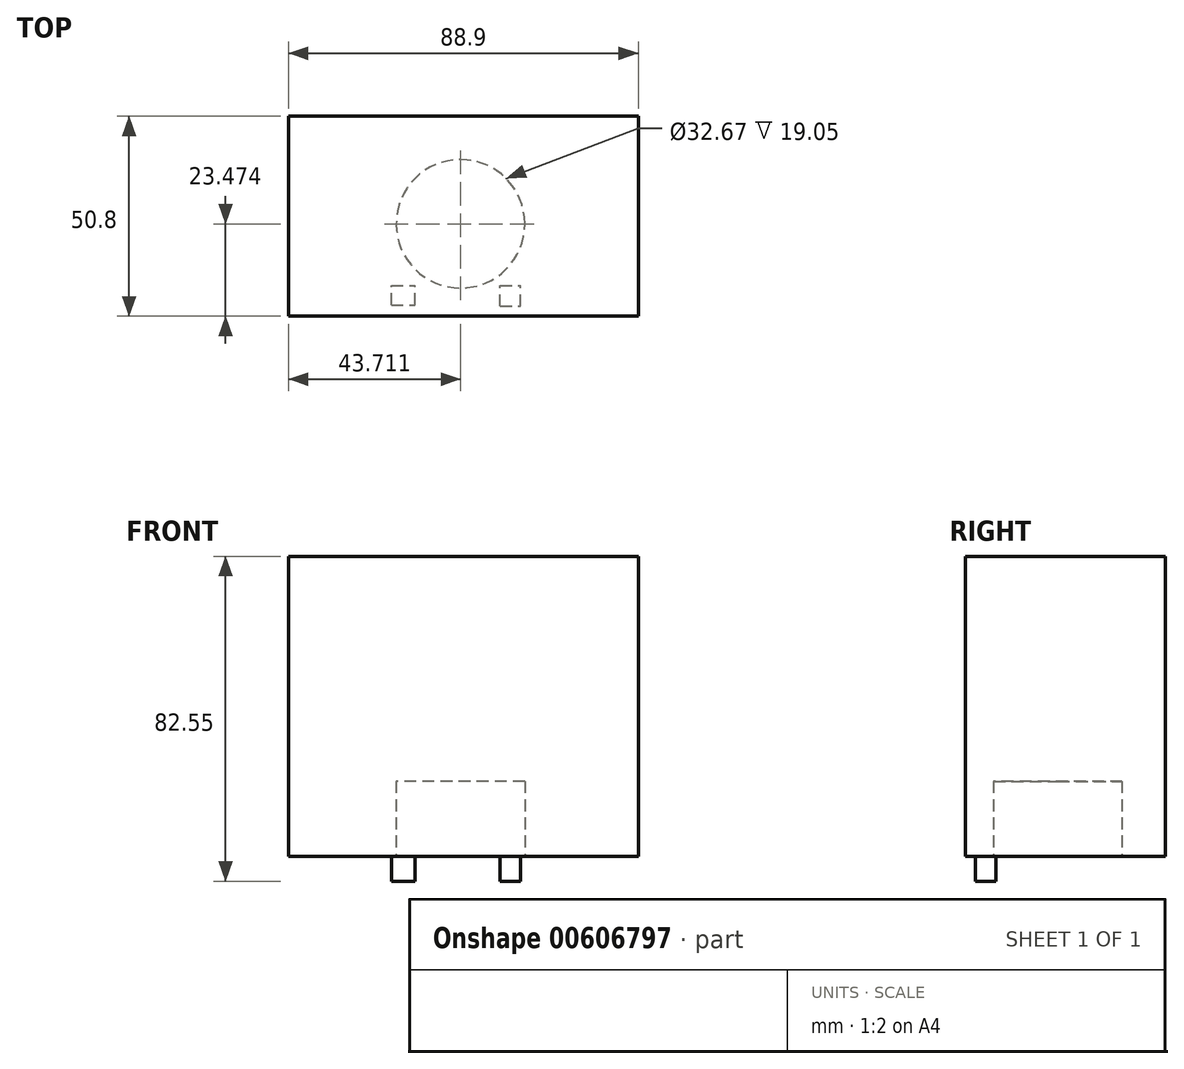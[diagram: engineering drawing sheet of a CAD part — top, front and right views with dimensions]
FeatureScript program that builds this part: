
annotation { "Feature Type Name" : "Feature", "Feature Type Description" : "" }
export const myFeature = defineFeature(function(context is Context, id is Id, definition is map)
    precondition{}
    {
        {
            var Q0;
            Q0=qCreatedBy(makeId("Top.planeOp"),FACE);
            var sketch = newSketch(context, id + "F0", { "sketchPlane" : qUnion([Q0])});
            skLineSegment(sketch, "E0.bottom", {"start": v(-48.46, 1.18) * mm, "end": v(40.44, 1.18) * mm});
            skLineSegment(sketch, "E0.top", {"start": v(-48.46, -49.62) * mm, "end": v(40.44, -49.62) * mm});
            skLineSegment(sketch, "E0.left", {"start": v(-48.46, 1.18) * mm, "end": v(-48.46, -49.62) * mm});
            skLineSegment(sketch, "E0.right", {"start": v(40.44, 1.18) * mm, "end": v(40.44, -49.62) * mm});
            skSolve(sketch);
        }
        {
            var Q0;
            Q0 = qSketchRegion(id + "F0", true);
            extrude(context, id + "F1", {"entities" : qUnion([Q0]), "depth" : 76.2 * mm, "offsetDistance" : 25.4 * mm});
        }
        {
            var Q0;
            Q0=qCreatedBy(makeId("Top.planeOp"),FACE);
            var sketch = newSketch(context, id + "F2", { "sketchPlane" : qUnion([Q0])});
            skCircle(sketch, "E1", {"center": v(-4.75, -26.15) * mm, "radius": 16.34 * mm});
            skSolve(sketch);
        }
        {
            var Q0;
            Q0 = qSketchRegion(id + "F2", true);
            extrude(context, id + "F3", {"entities" : qUnion([Q0]), "operationType" : NewBodyOperationType.REMOVE, "depth" : 19.05 * mm, "offsetDistance" : 25.4 * mm});
        }
        {
            var Q0;
            Q0=qCreatedBy(makeId("Top.planeOp"),FACE);
            var sketch = newSketch(context, id + "F4", { "sketchPlane" : qUnion([Q0])});
            skLineSegment(sketch, "E2.bottom", {"start": v(-24.32, -46.48) * mm, "end": v(-19.43, -46.48) * mm});
            skLineSegment(sketch, "E2.top", {"start": v(-24.32, -41.88) * mm, "end": v(-19.43, -41.88) * mm});
            skLineSegment(sketch, "E2.left", {"start": v(-24.32, -46.48) * mm, "end": v(-24.32, -41.88) * mm});
            skLineSegment(sketch, "E2.right", {"start": v(-19.43, -46.48) * mm, "end": v(-19.43, -41.88) * mm});
            skLineSegment(sketch, "E3.bottom", {"start": v(7.63, -46.2) * mm, "end": v(11.94, -46.2) * mm});
            skLineSegment(sketch, "E3.top", {"start": v(7.63, -42.16) * mm, "end": v(11.94, -42.16) * mm});
            skLineSegment(sketch, "E3.left", {"start": v(7.63, -46.2) * mm, "end": v(7.63, -42.16) * mm});
            skLineSegment(sketch, "E3.right", {"start": v(11.94, -46.2) * mm, "end": v(11.94, -42.16) * mm});
            skSolve(sketch);
        }
        {
            var Q0;
            Q0 = qSketchRegion(id + "F4", true);
            extrude(context, id + "F5", {"entities" : qUnion([Q0]), "operationType" : NewBodyOperationType.ADD, "depth" : 12.7 * mm, "offsetDistance" : 25.4 * mm});
        }
        {
            var Q0;
            Q0=qCreatedBy(makeId("Top.planeOp"),FACE);
            var sketch = newSketch(context, id + "F6", { "sketchPlane" : qUnion([Q0])});
            skLineSegment(sketch, "E4.bottom", {"start": v(-22.3, -46.77) * mm, "end": v(-16.26, -46.77) * mm});
            skLineSegment(sketch, "E4.top", {"start": v(-22.3, -41.88) * mm, "end": v(-16.26, -41.88) * mm});
            skLineSegment(sketch, "E4.left", {"start": v(-22.3, -46.77) * mm, "end": v(-22.3, -41.88) * mm});
            skLineSegment(sketch, "E4.right", {"start": v(-16.26, -46.77) * mm, "end": v(-16.26, -41.88) * mm});
            skLineSegment(sketch, "E5.bottom", {"start": v(5.32, -47.06) * mm, "end": v(10.5, -47.06) * mm});
            skLineSegment(sketch, "E5.top", {"start": v(5.32, -41.88) * mm, "end": v(10.5, -41.88) * mm});
            skLineSegment(sketch, "E5.left", {"start": v(5.32, -47.06) * mm, "end": v(5.32, -41.88) * mm});
            skLineSegment(sketch, "E5.right", {"start": v(10.5, -47.06) * mm, "end": v(10.5, -41.88) * mm});
            skSolve(sketch);
        }
        {
            var Q0;
            Q0 = qSketchRegion(id + "F6", true);
            extrude(context, id + "F7", {"entities" : qUnion([Q0]), "operationType" : NewBodyOperationType.ADD, "oppositeDirection" : true, "depth" : 6.35 * mm, "offsetDistance" : 25.4 * mm});
        }
    });
